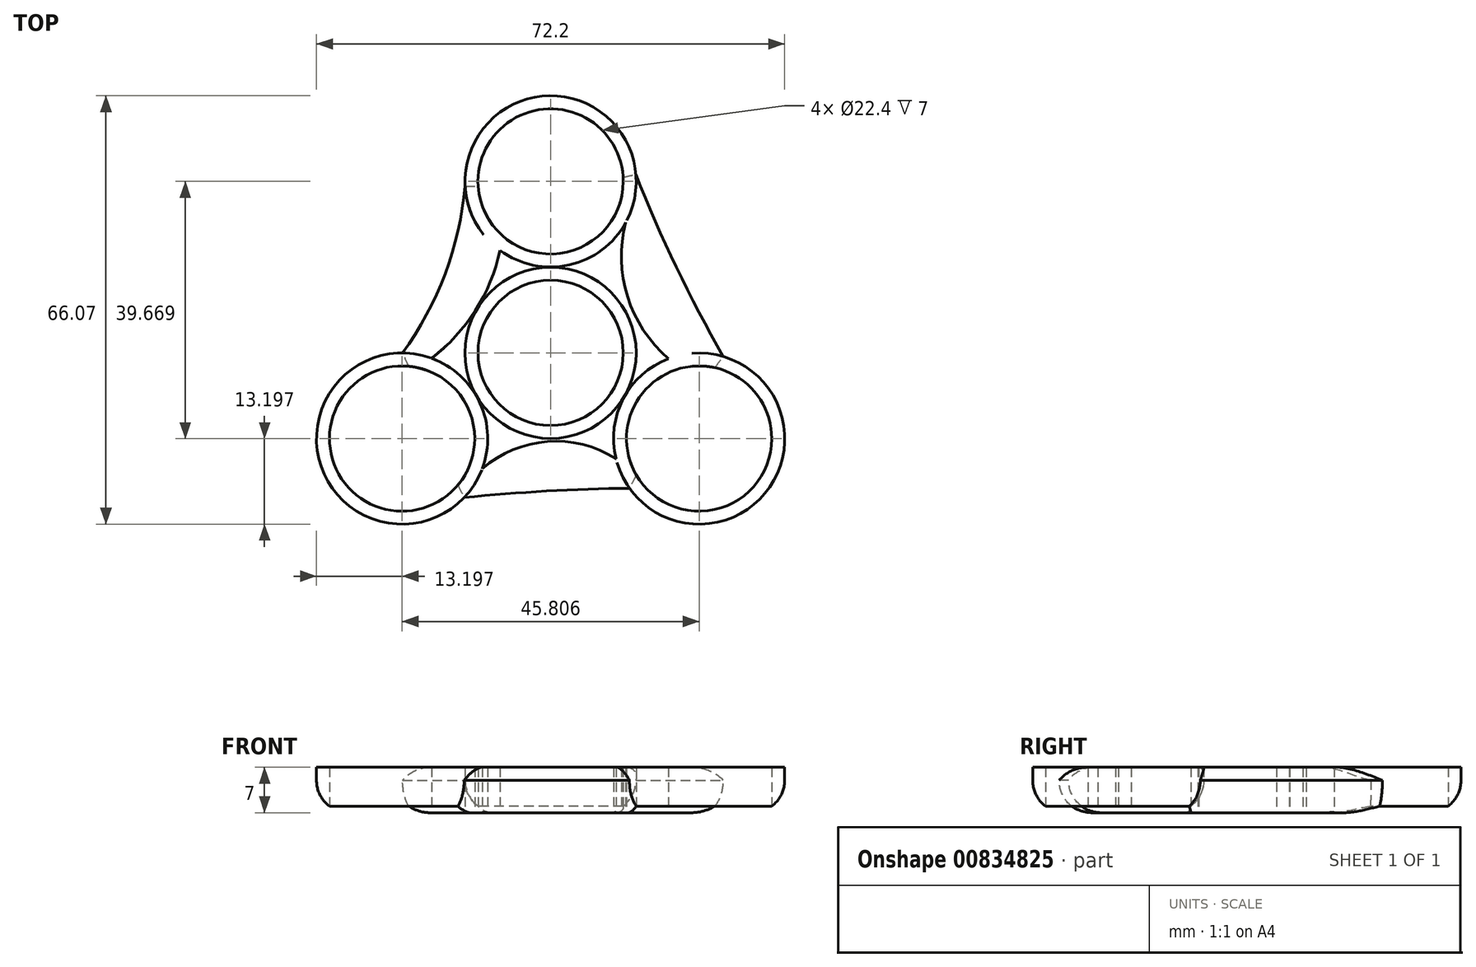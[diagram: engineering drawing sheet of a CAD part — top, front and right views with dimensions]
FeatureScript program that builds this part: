
annotation { "Feature Type Name" : "Feature", "Feature Type Description" : "" }
export const myFeature = defineFeature(function(context is Context, id is Id, definition is map)
    precondition{}
    {
        {
            var Q0;
            Q0=qCreatedBy(makeId("Top.planeOp"),FACE);
            var sketch = newSketch(context, id + "F0", { "sketchPlane" : qUnion([Q0])});
            skCircle(sketch, "E0", {"center": v(0, 0) * mm, "radius": 11.2 * mm});
            skCircle(sketch, "E1", {"center": v(0, 0) * mm, "radius": 13.2 * mm});
            skCircle(sketch, "E2", {"center": v(0, 26.45) * mm, "radius": 11.2 * mm});
            skCircle(sketch, "E3", {"center": v(0, 26.45) * mm, "radius": 13.2 * mm});
            skCircle(sketch, "E4.1.0", {"center": v(-22.9, -13.22) * mm, "radius": 11.2 * mm});
            skCircle(sketch, "E4.1.1", {"center": v(-22.9, -13.22) * mm, "radius": 13.2 * mm});
            skCircle(sketch, "E4.2.0", {"center": v(22.9, -13.22) * mm, "radius": 11.2 * mm});
            skCircle(sketch, "E4.2.1", {"center": v(22.9, -13.22) * mm, "radius": 13.2 * mm});
            skArc(sketch, "E5", {"start": v(-18.35, -0.83) * mm, "mid": v(-11.6, 6.54) * mm, "end": v(-7.8, 15.8) * mm});
            skArc(sketch, "E6", {"start": v(10.08, -16.34) * mm, "mid": v(-0.5, -13.68) * mm, "end": v(-10.55, -17.88) * mm});
            skArc(sketch, "E7", {"start": v(11.58, 20.12) * mm, "mid": v(11.87, 8.66) * mm, "end": v(18.18, -0.9) * mm});
            skArc(sketch, "E8", {"start": v(13.16, 27.53) * mm, "mid": v(19.38, 13.24) * mm, "end": v(26.64, -0.56) * mm});
            skArc(sketch, "E9", {"start": v(-22.84, -0.02) * mm, "mid": v(-16.27, 12.2) * mm, "end": v(-13.18, 25.72) * mm});
            skArc(sketch, "E10", {"start": v(12.15, -20.88) * mm, "mid": v(-0.61, -21.32) * mm, "end": v(-13.34, -22.32) * mm});
            skSolve(sketch);
        }
        {
            var Q0;
            Q0 = qSketchRegion(id + "F0", true);
            var Q1;
            Q1=makeQuery(id+"F0.imprint","IMPRINT",FACE,{"disambiguationData":[TD([[makeQuery(id+"F0.imprint","IMPRINT",EDGE,{"derivedFrom":sQuery(id+"F0.wireOp",EDGE,"E0")}),-1.0]])]});
            extrude(context, id + "F1", {"entities" : qUnion([Q0, Q1]), "depth" : 7 * mm, "offsetDistance" : 25 * mm});
        }
        {
            var Q0;
            {var subQ0=sQuery(id+"F0.wireOp",EDGE,"E3");Q0=makeQuery(id+"F1.opExtrude","CAP_EDGE",EDGE,{"disambiguationData":[OSD([subQ0]),TDD([makeQuery(id+"F0.imprint","IMPRINT",EDGE,{"disambiguationData":[TD([[makeQuery(id+"F0.imprint","INTERSECT",VERTEX,{"derivedFrom":[subQ0,sQuery(id+"F0.wireOp",EDGE,"E8")]}),-1.0]])],"derivedFrom":subQ0})])],"isStart":true});}
            var Q1;
            Q1=makeQuery(id+"F1.opExtrude","CAP_EDGE",EDGE,{"disambiguationData":[OSD([sQuery(id+"F0.wireOp",EDGE,"E8")])],"isStart":true});
            var Q2;
            {var subQ0=sQuery(id+"F0.wireOp",EDGE,"E4.2.1");Q2=makeQuery(id+"F1.opExtrude","CAP_EDGE",EDGE,{"disambiguationData":[OSD([subQ0]),TDD([makeQuery(id+"F0.imprint","IMPRINT",EDGE,{"disambiguationData":[TD([[makeQuery(id+"F0.imprint","INTERSECT",VERTEX,{"derivedFrom":[subQ0,sQuery(id+"F0.wireOp",EDGE,"E8")]}),1.0]])],"derivedFrom":subQ0})])],"isStart":true});}
            var Q3;
            Q3=makeQuery(id+"F1.opExtrude","CAP_EDGE",EDGE,{"disambiguationData":[OSD([sQuery(id+"F0.wireOp",EDGE,"E10")])],"isStart":true});
            var Q4;
            {var subQ0=sQuery(id+"F0.wireOp",EDGE,"E4.1.1");Q4=makeQuery(id+"F1.opExtrude","CAP_EDGE",EDGE,{"disambiguationData":[OSD([subQ0]),TDD([makeQuery(id+"F0.imprint","IMPRINT",EDGE,{"disambiguationData":[TD([[makeQuery(id+"F0.imprint","INTERSECT",VERTEX,{"derivedFrom":[subQ0,sQuery(id+"F0.wireOp",EDGE,"E9")]}),-1.0]])],"derivedFrom":subQ0})])],"isStart":true});}
            var Q5;
            Q5=makeQuery(id+"F1.opExtrude","CAP_EDGE",EDGE,{"disambiguationData":[OSD([sQuery(id+"F0.wireOp",EDGE,"E9")])],"isStart":true});
            fillet(context, id + "F2", {"entities" : qUnion([Q0, Q1, Q2, Q3, Q4, Q5]), "radius" : 5 * mm, "tangentPropagation" : true, "allowEdgeOverflow" : false});
        }
        {
            var Q0;
            Q0=makeQuery(id+"F1.opExtrude","CAP_EDGE",EDGE,{"disambiguationData":[OSD([sQuery(id+"F0.wireOp",EDGE,"E8")])],"isStart":false});
            var Q1;
            Q1=makeQuery(id+"F1.opExtrude","CAP_EDGE",EDGE,{"disambiguationData":[OSD([sQuery(id+"F0.wireOp",EDGE,"E9")])],"isStart":false});
            var Q2;
            Q2=makeQuery(id+"F1.opExtrude","CAP_EDGE",EDGE,{"disambiguationData":[OSD([sQuery(id+"F0.wireOp",EDGE,"E10")])],"isStart":false});
            fillet(context, id + "F3", {"entities" : qUnion([Q0, Q1, Q2]), "radius" : 5 * mm, "tangentPropagation" : true, "allowEdgeOverflow" : false});
        }
    });
